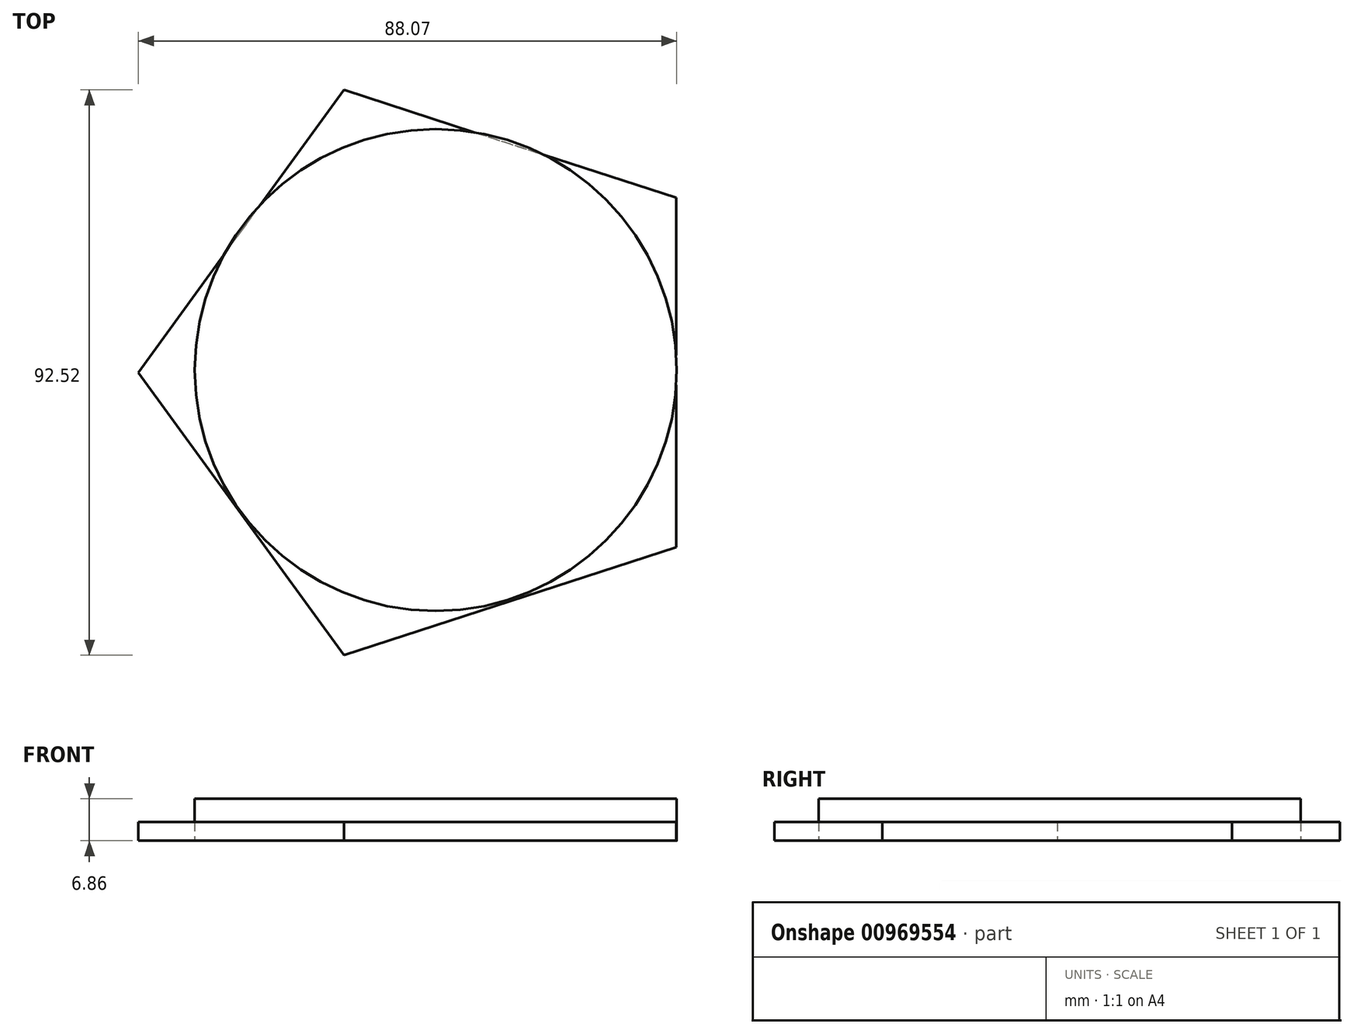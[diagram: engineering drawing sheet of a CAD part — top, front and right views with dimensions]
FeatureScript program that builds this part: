
annotation { "Feature Type Name" : "Feature", "Feature Type Description" : "" }
export const myFeature = defineFeature(function(context is Context, id is Id, definition is map)
    precondition{}
    {
        {
            var Q0;
            Q0=qCreatedBy(makeId("Top.planeOp"),FACE);
            var sketch = newSketch(context, id + "F0", { "sketchPlane" : qUnion([Q0])});
            skCircle(sketch, "E0.cCircle", {"center": v(-20.38, 26.3) * mm, "radius": 39.35 * mm, "construction": true});
            skLineSegment(sketch, "E0.0", {"start": v(18.97, 54.9) * mm, "end": v(18.97, -2.29) * mm});
            skLineSegment(sketch, "E0.1", {"start": v(18.97, -2.29) * mm, "end": v(-35.41, -19.96) * mm});
            skLineSegment(sketch, "E0.2", {"start": v(-35.41, -19.96) * mm, "end": v(-69.02, 26.3) * mm});
            skLineSegment(sketch, "E0.3", {"start": v(-69.02, 26.3) * mm, "end": v(-35.41, 72.56) * mm});
            skLineSegment(sketch, "E0.4", {"start": v(-35.41, 72.56) * mm, "end": v(18.97, 54.9) * mm});
            skPoint(sketch, "E0.0.midPoint", {"position": v(18.97, 26.3) * mm});
            skSolve(sketch);
        }
        {
            var Q0;
            Q0=qCreatedBy(makeId("Top.planeOp"),FACE);
            var sketch = newSketch(context, id + "F1", { "sketchPlane" : qUnion([Q0])});
            skCircle(sketch, "E1", {"center": v(-20.38, 26.7) * mm, "radius": 39.43 * mm});
            skSolve(sketch);
        }
        {
            var Q0;
            Q0=makeQuery(id+"F0.imprint","IMPRINT",FACE,{"disambiguationData":[TD([[makeQuery(id+"F0.imprint","IMPRINT",EDGE,{"derivedFrom":sQuery(id+"F0.wireOp",EDGE,"E0.0")}),-1.0]])]});
            extrude(context, id + "F2", {"entities" : qUnion([Q0]), "depth" : 3.05 * mm, "offsetDistance" : 25.4 * mm});
        }
        {
            var Q0;
            Q0=makeQuery(id+"F1.imprint","IMPRINT",FACE,{"disambiguationData":[TD([[makeQuery(id+"F1.imprint","IMPRINT",EDGE,{"derivedFrom":sQuery(id+"F1.wireOp",EDGE,"E1")}),1.0]])]});
            extrude(context, id + "F3", {"entities" : qUnion([Q0]), "depth" : 6.86 * mm, "offsetDistance" : 25.4 * mm});
        }
    });
